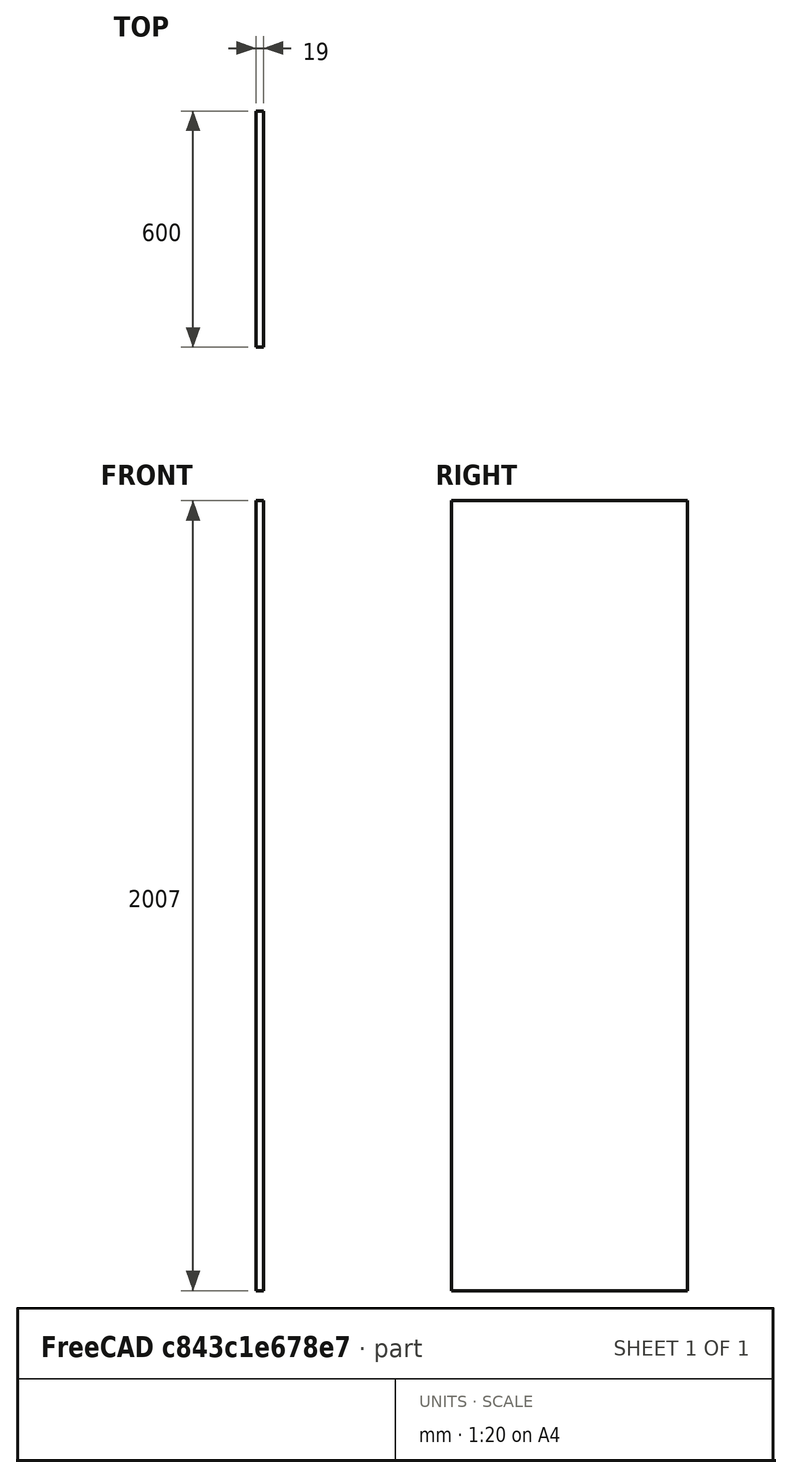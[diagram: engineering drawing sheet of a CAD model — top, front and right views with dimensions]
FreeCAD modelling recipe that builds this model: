
FCSTD DOCUMENT  (FreeCAD 1.0RUnknown)
Label: wardrobe_right_corpus00_jan
License: All rights reserved
LicenseURL: https://en.wikipedia.org/wiki/All_rights_reserved
objects: Sketcher::SketchObject×1, PartDesign::Pad×1, PartDesign::CoordinateSystem×1, PartDesign::Body×1
note: 7 computed .brp shape members not serialized (recipe doc carries the construction recipe); baked Part::Feature solids carry a one-line shape summary decoded from their .brp
EXTERNAL_REF file=../../mastersketch.FCStd obj=Spreadsheet

FEATURE [Sketcher::SketchObject] Sketch002
  ArcFitTolerance = 1e-06
  AttachmentSupport = -> [YZ_Plane004]
  FullyConstrained = true
  MakeInternals = true
  MapMode = 5
  Placement = pos=(0,0,0) rot=(0.57735,0.57735,0.57735;2.0944rad)
  expr: Constraints[10] = mastersketch#Spreadsheet.corpus_depth
  expr: Constraints[11] = mastersketch#Spreadsheet.corpus_height - 2 * mastersketch#Spreadsheet.corpus_outer_thickness
  sketch-geometry (5):
    g0: LineSegment StartX=-300 StartY=-1003.5 StartZ=0 EndX=300 EndY=-1003.5 EndZ=0
    g1: LineSegment StartX=300 StartY=-1003.5 StartZ=0 EndX=300 EndY=1003.5 EndZ=0
    g2: LineSegment StartX=300 StartY=1003.5 StartZ=0 EndX=-300 EndY=1003.5 EndZ=0
    g3: LineSegment StartX=-300 StartY=1003.5 StartZ=0 EndX=-300 EndY=-1003.5 EndZ=0
    g4: GeomPoint [constr] X=0 Y=0 Z=0
  constraints (12):
    c: Coincident(g0,g1)
    c: Coincident(g1,g2)
    c: Coincident(g2,g3)
    c: Coincident(g3,g0)
    c: Horizontal(g0)
    c: Horizontal(g2)
    c: Vertical(g1)
    c: Vertical(g3)
    c: Symmetric(g2,g0,g4)
    c: Coincident(g4,g-1)
    c: DistanceX(g0,g0) = 600
    c: DistanceY(g3,g3) = 2007
FEATURE [PartDesign::Pad] Pad002
  Direction = (1,0,0)
  Length = 19
  Length2 = 10
  Placement = pos=(0,0,0) rot=(1,1,1;2.0944rad)
  Profile = -> Sketch002
  ReferenceAxis = -> Sketch002 [N_Axis]
  Refine = true
  Suppressed = false
  Type = 0
  expr: Length = mastersketch#Spreadsheet.corpus_outer_thickness
FEATURE [PartDesign::CoordinateSystem] LCS_bottom
  AttacherType = Attacher::AttachEngine3D
  AttachmentSupport = -> [Pad002]
  MapMode = 45
  Placement = pos=(19,-1.82e-14,-1003.5) rot=(0,0.707107,0.707107;3.14159rad)
FEATURE [PartDesign::Body] Body002  label="wardrobe_right_corpus00_jan"
  AllowCompound = false
  Group = -> [Sketch002,Pad002,LCS_bottom]
  Origin = -> Origin004
  Tip = -> Pad002
